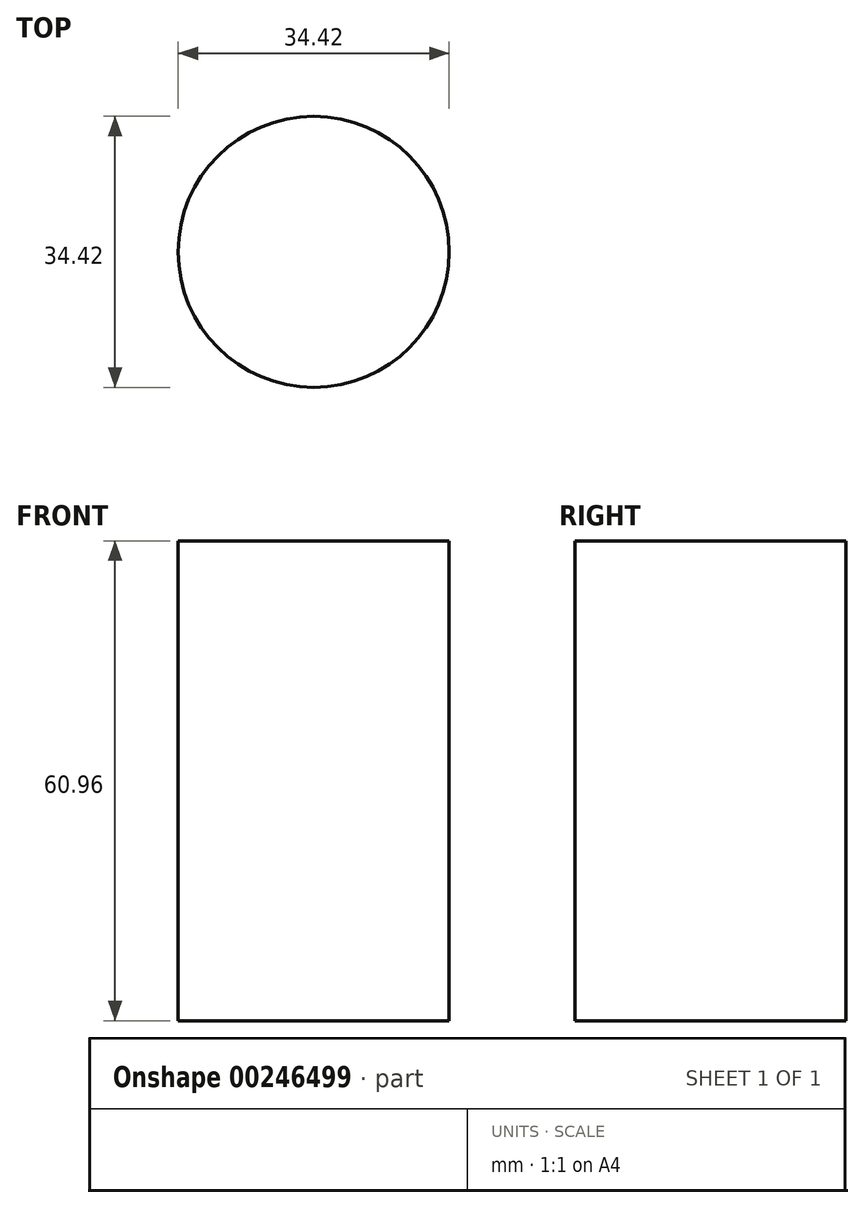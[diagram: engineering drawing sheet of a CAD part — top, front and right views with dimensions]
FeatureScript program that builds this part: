
annotation { "Feature Type Name" : "Feature", "Feature Type Description" : "" }
export const myFeature = defineFeature(function(context is Context, id is Id, definition is map)
    precondition{}
    {
        {
            var Q0;
            Q0=qCreatedBy(makeId("Top.planeOp"),FACE);
            var sketch = newSketch(context, id + "F0", { "sketchPlane" : qUnion([Q0])});
            skCircle(sketch, "E0", {"center": v(0, 0) * mm, "radius": 17.2 * mm});
            skSolve(sketch);
        }
        {
            var Q0;
            Q0 = qSketchRegion(id + "F0", true);
            extrude(context, id + "F1", {"entities" : qUnion([Q0]), "depth" : 60.96 * mm});
        }
    });
